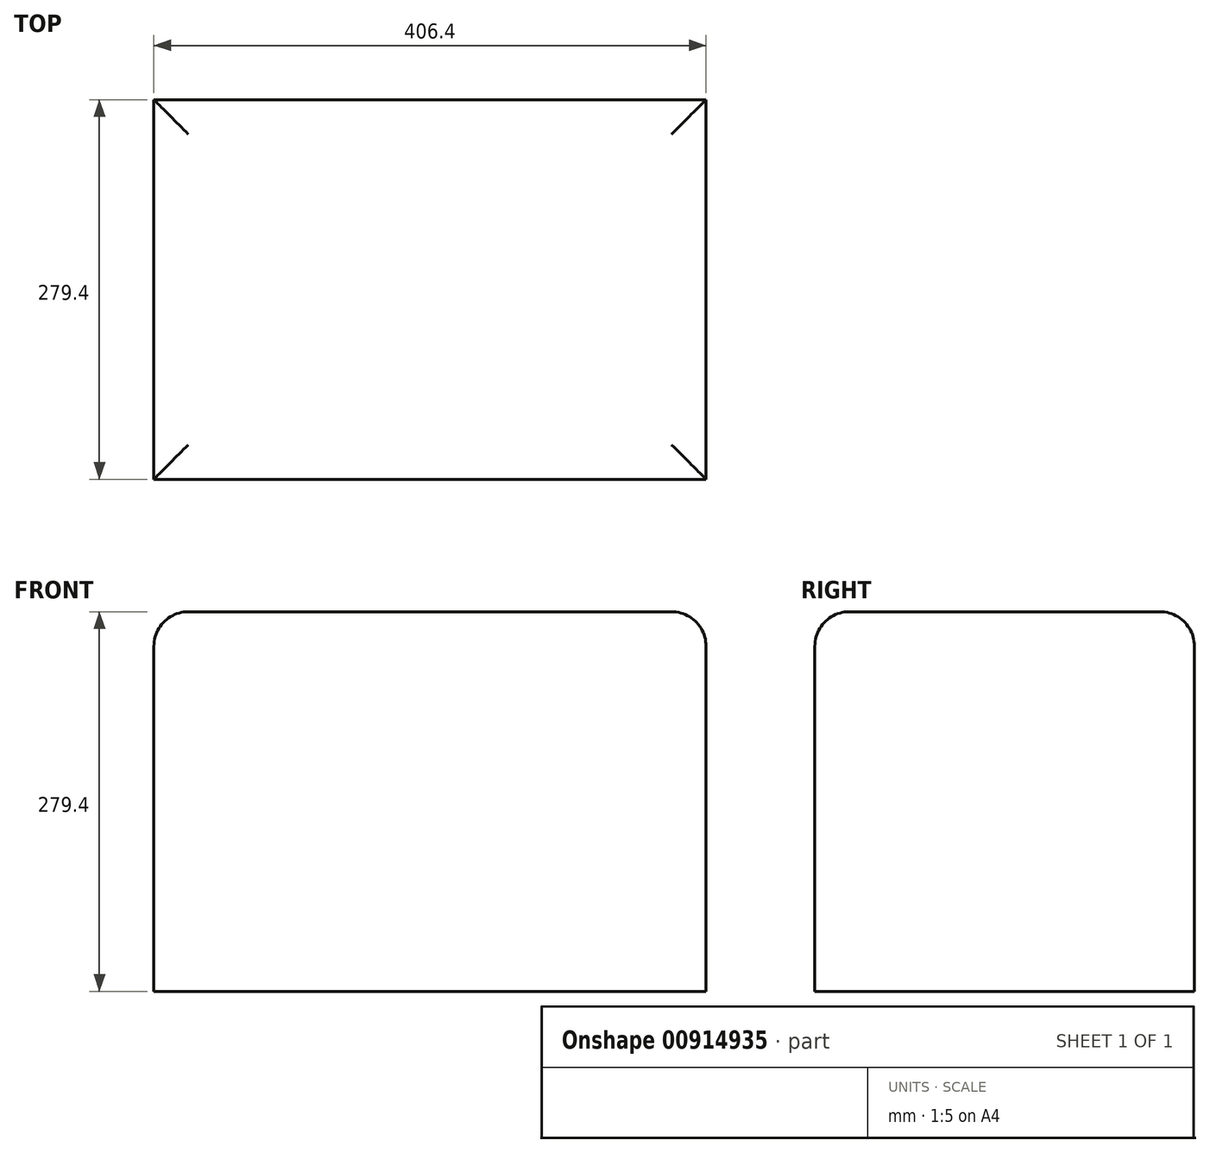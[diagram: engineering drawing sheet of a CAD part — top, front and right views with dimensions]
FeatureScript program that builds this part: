
annotation { "Feature Type Name" : "Feature", "Feature Type Description" : "" }
export const myFeature = defineFeature(function(context is Context, id is Id, definition is map)
    precondition{}
    {
        {
            var Q0;
            Q0=qCreatedBy(makeId("Top.planeOp"),FACE);
            var sketch = newSketch(context, id + "F0", { "sketchPlane" : qUnion([Q0])});
            skLineSegment(sketch, "E0.bottom", {"start": v(-363.37, 237.73) * mm, "end": v(43.03, 237.73) * mm});
            skLineSegment(sketch, "E0.top", {"start": v(-363.37, -41.67) * mm, "end": v(43.03, -41.67) * mm});
            skLineSegment(sketch, "E0.left", {"start": v(-363.37, 237.73) * mm, "end": v(-363.37, -41.67) * mm});
            skLineSegment(sketch, "E0.right", {"start": v(43.03, 237.73) * mm, "end": v(43.03, -41.67) * mm});
            skSolve(sketch);
        }
        {
            var Q0;
            Q0=makeQuery(id+"F0.imprint","IMPRINT",FACE,{"disambiguationData":[TD([[makeQuery(id+"F0.imprint","IMPRINT",EDGE,{"derivedFrom":sQuery(id+"F0.wireOp",EDGE,"E0.bottom")}),-1.0]])]});
            extrude(context, id + "F1", {"entities" : qUnion([Q0]), "depth" : 279.4 * mm, "offsetDistance" : 25.4 * mm});
        }
        {
            var Q0;
            Q0=makeQuery(id+"F1.opExtrude","CAP_EDGE",EDGE,{"disambiguationData":[OSD([sQuery(id+"F0.wireOp",EDGE,"E0.top")])],"isStart":false});
            var Q1;
            Q1=makeQuery(id+"F1.opExtrude","CAP_EDGE",EDGE,{"disambiguationData":[OSD([sQuery(id+"F0.wireOp",EDGE,"E0.left")])],"isStart":false});
            var Q2;
            Q2=makeQuery(id+"F1.opExtrude","CAP_EDGE",EDGE,{"disambiguationData":[OSD([sQuery(id+"F0.wireOp",EDGE,"E0.bottom")])],"isStart":false});
            var Q3;
            Q3=makeQuery(id+"F1.opExtrude","CAP_EDGE",EDGE,{"disambiguationData":[OSD([sQuery(id+"F0.wireOp",EDGE,"E0.right")])],"isStart":false});
            fillet(context, id + "F2", {"entities" : qUnion([Q0, Q1, Q2, Q3]), "radius" : 25.4 * mm, "tangentPropagation" : true, "allowEdgeOverflow" : false});
        }
    });
